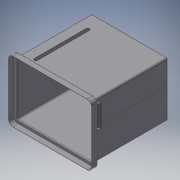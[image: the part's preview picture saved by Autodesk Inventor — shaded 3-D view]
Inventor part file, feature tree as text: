
AUTODESK INVENTOR PART (.ipt)
format: ipt  version: 2019 (Build 230136000, 136)  size: 349,696 bytes
history: native  units: in
note: dims shown in document units (in); Inventor stores cm internally (conversion verified against a paired STEP export)
features: extrude x10, sketch x10, projected_geometry x8, other x5, reference x4, fillet x3, helix x2
ambient origin geometry x8: Origin, YZ Plane, XZ Plane, XY Plane, X Axis, Y Axis, Z Axis, Center Point
bodies: Solid1 (feature_tree)
feature tree (42):
  extrude  "Extrusion1"  Depth=0.5906in
  extrude  "Extrusion2"  Depth=0.5906in
  fillet  "Fillet1"  Radius=0.0472in
  extrude  "Extrusion3"  Depth=11.811in
  fillet  "Fillet2"  Radius=0.7874in
  extrude  "Extrusion4"  Depth=5.5541in TaperAngle=0.0deg
  extrude  "Extrusion5"  Depth=0.0472in TaperAngle=0.0deg
  fillet  "Fillet3"  Radius=0.1969in
  extrude  "Extrusion6"  Depth=0.0472in
  extrude  "Extrusion8"  Depth=0.0472in TaperAngle=0.0deg
  extrude  "Extrusion9"  Depth=0.0472in TaperAngle=0.0deg
  extrude  "Extrusion10"  Depth=0.0472in TaperAngle=0.0deg
  extrude  "Extrusion11"  Depth=0.0472in TaperAngle=0.0deg
  sketch  "Sketch1"  dims[d0=0.5906in d1=0.5906in]
  reference  "Reference1"
  reference  "Reference2"
  reference  "Reference3"
  reference  "Reference4"
  sketch  "Sketch2"  dims[d2=0.5906in d3=0.5906in d4=0.0472in]
  sketch  "Sketch3"  dims[d5=16.9291in d6=0.0in d7=11.811in d8=0.7874in]
  projected_geometry  "Projected Loop1"
  sketch  "Sketch4"  dims[d9=1.5748in d10=5.5541in d11=0.0in]
  projected_geometry  "Projected Loop2"
  sketch  "Sketch5"  dims[d12=0.1969in d13=0.0472in d14=0.0in d15=0.1969in]
  projected_geometry  "Projected Loop3"
  projected_geometry  "Projected Loop4"
  sketch  "Sketch6"  dims[d16=0.7874in d17=0.0472in]
  projected_geometry  "Projected Loop5"
  sketch  "Sketch8"  dims[d18=1.1811in d19=0.0in d20=0.0472in d21=0.0in]
  sketch  "Sketch9"  dims[d22=0.1969in d23=0.0472in d24=0.0in]
  projected_geometry  "Projected Loop8"
  sketch  "Sketch10"  dims[d28=0.0472in d29=0.0in d30=0.0472in d31=0.0in]
  projected_geometry  "Projected Loop9"
  sketch  "Sketch11"  dims[d32=0.0472in d33=0.0in d36=0.0472in d37=0.0in]
  projected_geometry  "Projected Loop10"
  other  "<userpath>\Documents\CAD Files\Helix DLP\Helix DLP.iam"
  helix  "Helix DLP.iam"  [1 undecoded]
  helix  "Helix DLP Z Stage:1"  [1 undecoded]
  other  "Z stage_side:2"
  other  "Z stage_side:1"
  other  "Print Platform:1"
  other  "Z stage_brace:1"
note: 2 required parameter values undecoded (feature->parameter linkage not recoverable at this tier; creation-order binding heuristic only, values carry confidence <= 0.55)
